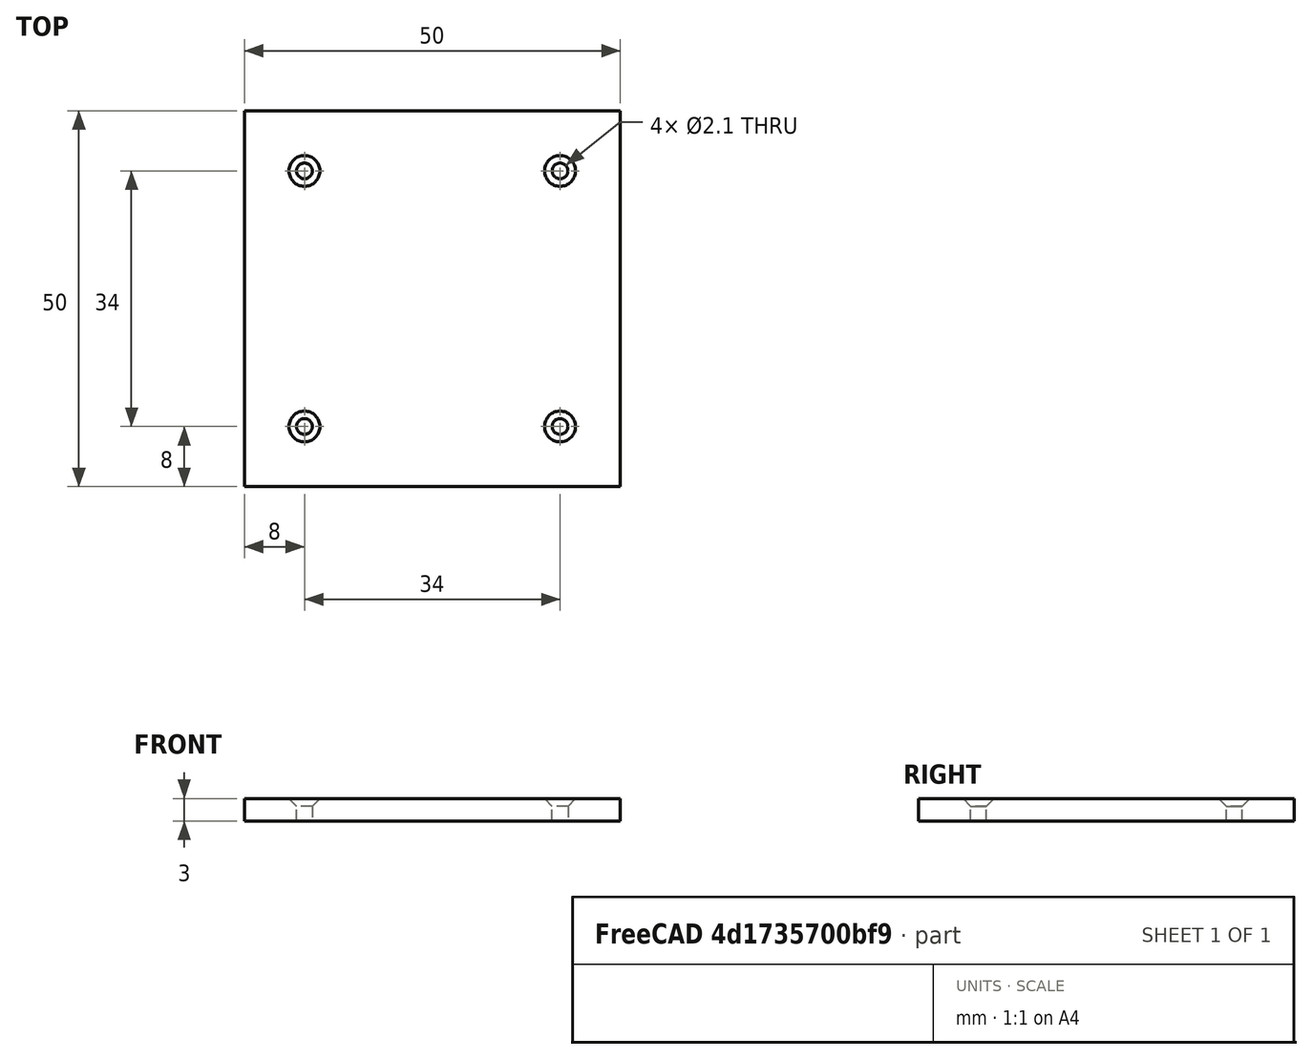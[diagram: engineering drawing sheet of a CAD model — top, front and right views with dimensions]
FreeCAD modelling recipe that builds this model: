
FCSTD DOCUMENT  (FreeCAD 0.21R33771 (Git))
Label: part2
License: All rights reserved
LicenseURL: http://en.wikipedia.org/wiki/All_rights_reserved
objects: TechDraw::DrawViewDimension×7, Sketcher::SketchObject×2, TechDraw::DrawProjGroupItem×2, PartDesign::Pad×1, PartDesign::Pocket×1, PartDesign::Chamfer×1, PartDesign::Body×1, TechDraw::DrawSVGTemplate×1, TechDraw::DrawViewPart×1, TechDraw::DrawProjGroup×1, TechDraw::DrawPage×1
note: 19 computed .brp shape members not serialized (recipe doc carries the construction recipe); baked Part::Feature solids carry a one-line shape summary decoded from their .brp

FEATURE [Sketcher::SketchObject] Sketch
  FullyConstrained = true
  MapMode = 5
  Support = -> [XY_Plane]
  sketch-geometry (5):
    g0: LineSegment StartX=-25 StartY=-25 StartZ=0 EndX=-25 EndY=25 EndZ=0
    g1: LineSegment StartX=-25 StartY=25 StartZ=0 EndX=25 EndY=25 EndZ=0
    g2: LineSegment StartX=25 StartY=25 StartZ=0 EndX=25 EndY=-25 EndZ=0
    g3: LineSegment StartX=25 StartY=-25 StartZ=0 EndX=-25 EndY=-25 EndZ=0
    g4: GeomPoint X=0 Y=0 Z=0
  constraints (12):
    c: Coincident(g0,g1)
    c: Coincident(g1,g2)
    c: Coincident(g2,g3)
    c: Coincident(g3,g0)
    c: Horizontal(g1)
    c: Horizontal(g3)
    c: Vertical(g0)
    c: Vertical(g2)
    c: Symmetric(g1,g0,g4)
    c: Coincident(g4,g-1)
    c: DistanceX(g1,g1) = 50
    c: DistanceY(g2,g2) = 50
FEATURE [PartDesign::Pad] Pad
  Direction = (0,0,1)
  Length = 3
  Length2 = 10
  Profile = -> Sketch
  ReferenceAxis = -> Sketch [N_Axis]
  Type = 0
FEATURE [Sketcher::SketchObject] Sketch001
  ExternalGeometry = -> [Pad]
  FullyConstrained = true
  MapMode = 5
  Placement = pos=(0,0,3) rot=(0,0,1;0rad)
  Support = -> [Pad]
  sketch-geometry (4):
    g0: Circle CenterX=-17 CenterY=17 CenterZ=0 NormalX=0 NormalY=0 NormalZ=1 AngleXU=0 Radius=1.05
    g1: Circle CenterX=17 CenterY=17 CenterZ=0 NormalX=0 NormalY=0 NormalZ=1 AngleXU=0 Radius=1.05
    g2: Circle CenterX=17 CenterY=-17 CenterZ=0 NormalX=0 NormalY=0 NormalZ=1 AngleXU=0 Radius=1.05
    g3: Circle CenterX=-17 CenterY=-17 CenterZ=0 NormalX=0 NormalY=0 NormalZ=1 AngleXU=0 Radius=1.05
  constraints (12):
    c: Diameter(g0) = 2.1
    c: Equal(g0,g1)
    c: Equal(g1,g2)
    c: Equal(g2,g3)
    c: DistanceX(g-3,g0) = 8
    c: DistanceY(g0,g-3) = 8
    c: Horizontal(g0,g1)
    c: Horizontal(g3,g2)
    c: Vertical(g3,g0)
    c: Vertical(g2,g1)
    c: DistanceX(g2,g-4) = 8
    c: DistanceY(g-4,g2) = 8
FEATURE [PartDesign::Pocket] Pocket
  BaseFeature = -> Pad
  Direction = (0,0,-1)
  Length = 5
  Length2 = 5
  Profile = -> Sketch001
  ReferenceAxis = -> Sketch001 [N_Axis]
  Type = 1
FEATURE [PartDesign::Chamfer] Chamfer
  Angle = 45
  Base = -> Pocket [Edge19,Edge20,Edge18,Edge17]
  BaseFeature = -> Pocket
  ChamferType = 0
  FlipDirection = false
  Size = 1
  Size2 = 1
  SupportTransform = false
  UseAllEdges = false
FEATURE [PartDesign::Body] Body
  Group = -> [Sketch,Pad,Sketch001,Pocket,Chamfer]
  Origin = -> Origin
  Tip = -> Chamfer
FEATURE [TechDraw::DrawSVGTemplate] Template
  EditableTexts = Designed_by_Name=Reza Heshmati; Drawing_number=Drawing number; FC-Date=Date; FC-SC=Scale; FC-SH=Sheet; FC-Title=Item #5 (part 2); Subtitle=Subtitle; Weight=Weight
  Height = 210
  Orientation = 1
  Template = <path>
  Width = 297
FEATURE [TechDraw::DrawViewPart] View
  CoarseView = false
  Direction = (0.57735,-0.57735,0.57735)
  Focus = 100
  HardHidden = false
  IsoCount = 0
  IsoHidden = false
  IsoVisible = false
  LockPosition = false
  Perspective = false
  Rotation = 0
  ScaleType = 0
  ScrubCount = 0
  SeamHidden = false
  SeamVisible = false
  SmoothHidden = false
  SmoothVisible = true
  Source = -> [Chamfer]
  X = 66.6149
  XDirection = (0.707107,0.707107,0)
  Y = 155.836
FEATURE [TechDraw::DrawProjGroupItem] ProjItem  label="Front"
  Caption = Top View
  CoarseView = false
  Direction = (0,0,1)
  Focus = 100
  HardHidden = false
  IsoCount = 0
  IsoHidden = false
  IsoVisible = false
  LockPosition = true
  Perspective = false
  Rotation = 0
  RotationVector = (1,0,0)
  ScaleType = 2
  ScrubCount = 0
  SeamHidden = false
  SeamVisible = false
  SmoothHidden = false
  SmoothVisible = true
  Source = -> [Chamfer]
  Type = 0
  X = 0
  XDirection = (1,0,0)
  Y = 0
FEATURE [TechDraw::DrawProjGroupItem] ProjItem002  label="Bottom"
  Caption = Side View
  CoarseView = false
  Direction = (0,-1,0)
  Focus = 100
  HardHidden = false
  IsoCount = 0
  IsoHidden = false
  IsoVisible = false
  LockPosition = false
  Perspective = false
  Rotation = 0
  RotationVector = (1,0,0)
  ScaleType = 2
  ScrubCount = 0
  SeamHidden = false
  SeamVisible = false
  SmoothHidden = false
  SmoothVisible = true
  Source = -> [Chamfer]
  Type = 5
  X = 0
  XDirection = (1,0,0)
  Y = 51.5
FEATURE [TechDraw::DrawProjGroup] ProjGroup
  Anchor = -> ProjItem
  AutoDistribute = true
  LockPosition = false
  ProjectionType = 0
  Rotation = 0
  ScaleType = 0
  Source = -> [Chamfer]
  Views = -> [ProjItem,ProjItem002]
  X = 202.989
  Y = 117.481
  spacingX = 15
  spacingY = 25
FEATURE [TechDraw::DrawViewDimension] Dimension
  AngleOverride = false
  Arbitrary = false
  ArbitraryTolerances = false
  EqualTolerance = true
  ExtensionAngle = 0
  FormatSpec = %.2w
  FormatSpecOverTolerance = %+.2w
  FormatSpecUnderTolerance = %+.2w
  Inverted = false
  LineAngle = 0
  LockPosition = false
  MeasureType = 1
  OverTolerance = 0
  References2D = -> [ProjItem002]
  Rotation = 0
  ScaleType = 0
  TheoreticalExact = false
  Type = 2
  UnderTolerance = 0
  X = -34.7333
  Y = 3.74444
FEATURE [TechDraw::DrawViewDimension] Dimension001
  AngleOverride = false
  Arbitrary = false
  ArbitraryTolerances = false
  EqualTolerance = true
  ExtensionAngle = 0
  FormatSpec = %.2w
  FormatSpecOverTolerance = %+.2w
  FormatSpecUnderTolerance = %+.2w
  Inverted = false
  LineAngle = 0
  LockPosition = false
  MeasureType = 1
  OverTolerance = 0
  References2D = -> [ProjItem]
  Rotation = 0
  ScaleType = 0
  TheoreticalExact = false
  Type = 1
  UnderTolerance = 0
  X = -0.441617
  Y = 34.7867
FEATURE [TechDraw::DrawViewDimension] Dimension002
  AngleOverride = false
  Arbitrary = false
  ArbitraryTolerances = false
  EqualTolerance = true
  ExtensionAngle = 0
  FormatSpec = %.2w
  FormatSpecOverTolerance = %+.2w
  FormatSpecUnderTolerance = %+.2w
  Inverted = false
  LineAngle = 0
  LockPosition = false
  MeasureType = 1
  OverTolerance = 0
  References2D = -> [ProjItem]
  Rotation = 0
  ScaleType = 0
  TheoreticalExact = false
  Type = 2
  UnderTolerance = 0
  X = -32.0659
  Y = 2.72081
FEATURE [TechDraw::DrawViewDimension] Dimension003
  AngleOverride = false
  Arbitrary = false
  ArbitraryTolerances = false
  EqualTolerance = true
  ExtensionAngle = 0
  FormatSpec = ⌀%.2w
  FormatSpecOverTolerance = %+.2w
  FormatSpecUnderTolerance = %+.2w
  Inverted = false
  LineAngle = 0
  LockPosition = false
  MeasureType = 1
  OverTolerance = 0
  References2D = -> [ProjItem]
  Rotation = 0
  ScaleType = 0
  TheoreticalExact = false
  Type = 5
  UnderTolerance = 0
  X = -5.11942
  Y = 23.612
FEATURE [TechDraw::DrawViewDimension] Dimension004
  AngleOverride = false
  Arbitrary = false
  ArbitraryTolerances = false
  EqualTolerance = true
  ExtensionAngle = 0
  FormatSpec = ⌀%.2w
  FormatSpecOverTolerance = %+.2w
  FormatSpecUnderTolerance = %+.2w
  Inverted = false
  LineAngle = 0
  LockPosition = false
  MeasureType = 1
  OverTolerance = 0
  References2D = -> [ProjItem]
  Rotation = 0
  ScaleType = 0
  TheoreticalExact = false
  Type = 5
  UnderTolerance = 0
  X = -6.05972
  Y = 14.8359
FEATURE [TechDraw::DrawViewDimension] Dimension005
  AngleOverride = false
  Arbitrary = false
  ArbitraryTolerances = false
  EqualTolerance = true
  ExtensionAngle = 0
  FormatSpec = %.2w
  FormatSpecOverTolerance = %+.2w
  FormatSpecUnderTolerance = %+.2w
  Inverted = false
  LineAngle = 0
  LockPosition = false
  MeasureType = 1
  OverTolerance = 0
  References2D = -> [ProjItem]
  Rotation = 0
  ScaleType = 0
  TheoreticalExact = false
  Type = 2
  UnderTolerance = 0
  X = 30.7664
  Y = 23.0821
FEATURE [TechDraw::DrawViewDimension] Dimension006
  AngleOverride = false
  Arbitrary = false
  ArbitraryTolerances = false
  EqualTolerance = true
  ExtensionAngle = 0
  FormatSpec = %.2w
  FormatSpecOverTolerance = %+.2w
  FormatSpecUnderTolerance = %+.2w
  Inverted = false
  LineAngle = 0
  LockPosition = false
  MeasureType = 1
  OverTolerance = 0
  References2D = -> [ProjItem]
  Rotation = 0
  ScaleType = 0
  TheoreticalExact = false
  Type = 1
  UnderTolerance = 0
  X = 21.1045
  Y = 38.6993
FEATURE [TechDraw::DrawPage] Page
  KeepUpdated = true
  NextBalloonIndex = 1
  ProjectionType = 0
  Template = -> Template
  Views = -> [View,ProjGroup,Dimension,Dimension001,Dimension002,Dimension003,Dimension004,Dimension005,Dimension006]
note: 1 file-system path scrubbed to <path> (originals preserved in the JSON sidecar)
